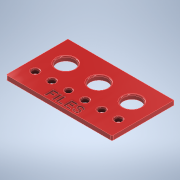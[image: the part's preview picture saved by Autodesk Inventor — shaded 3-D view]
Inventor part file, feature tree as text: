
AUTODESK INVENTOR PART (.ipt)
format: ipt  version: 2021 (Build 250183000, 183)  size: 294,912 bytes
history: native  units: in
note: dims shown in document units (in); Inventor stores cm internally (conversion verified against a paired STEP export)
features: extrude x3, fillet x2, sketch x2
ambient origin geometry x8: Origin, YZ Plane, XZ Plane, XY Plane, X Axis, Y Axis, Z Axis, Center Point
bodies: Solid1 (feature_tree)
feature tree (7):
  extrude  "Extrusion1"  Depth=1.0in
  extrude  "Extrusion3"  Depth=0.0625in
  extrude  "Extrusion5"  Depth=0.0625in
  fillet  "Fillet5"  Radius=0.1in
  fillet  "Fillet6"  Radius=0.0625in
  sketch  "Sketch1"  dims[d1=0.0in d16=1.0in]
  sketch  "Sketch8"  dims[d38=0.0in d39=0.0in d53=1.125in d57=0.4677in d58=0.1in d59=0.0in d60=0.0625in d61=0.0625in d51=0.5in d52=0.0344in d54=0.0344in]
